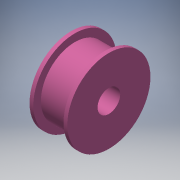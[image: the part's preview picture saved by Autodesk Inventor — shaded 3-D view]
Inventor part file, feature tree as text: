
AUTODESK INVENTOR PART (.ipt)
format: ipt  version: 2017 SP1 (Build 210196100, 196)  size: 140,288 bytes
history: native  units: in
note: dims shown in document units (in); Inventor stores cm internally (conversion verified against a paired STEP export)
features: extrude x4, sketch x4
ambient origin geometry x8: Origin, YZ Plane, XZ Plane, XY Plane, X Axis, Y Axis, Z Axis, Center Point
bodies: Solid1 (feature_tree)
feature tree (8):
  extrude  "Extrusion1"  Depth=0.375in
  extrude  "Extrusion2"  Depth=0.5in
  extrude  "Extrusion3"  Depth=0.0625in TaperAngle=0.0deg
  extrude  "Extrusion4"  Depth=0.1875in TaperAngle=0.0deg
  sketch  "Sketch1"  dims[d0=1.125in d2=0.375in]
  sketch  "Sketch2"  dims[d4=0.5in d5=0.0in d6=0.125in]
  sketch  "Sketch3"  dims[d7=0.0625in d8=0.0in d9=0.0625in d10=0.0in]
  sketch  "Sketch4"  dims[d11=0.1875in d12=0.375in d13=0.0in]
